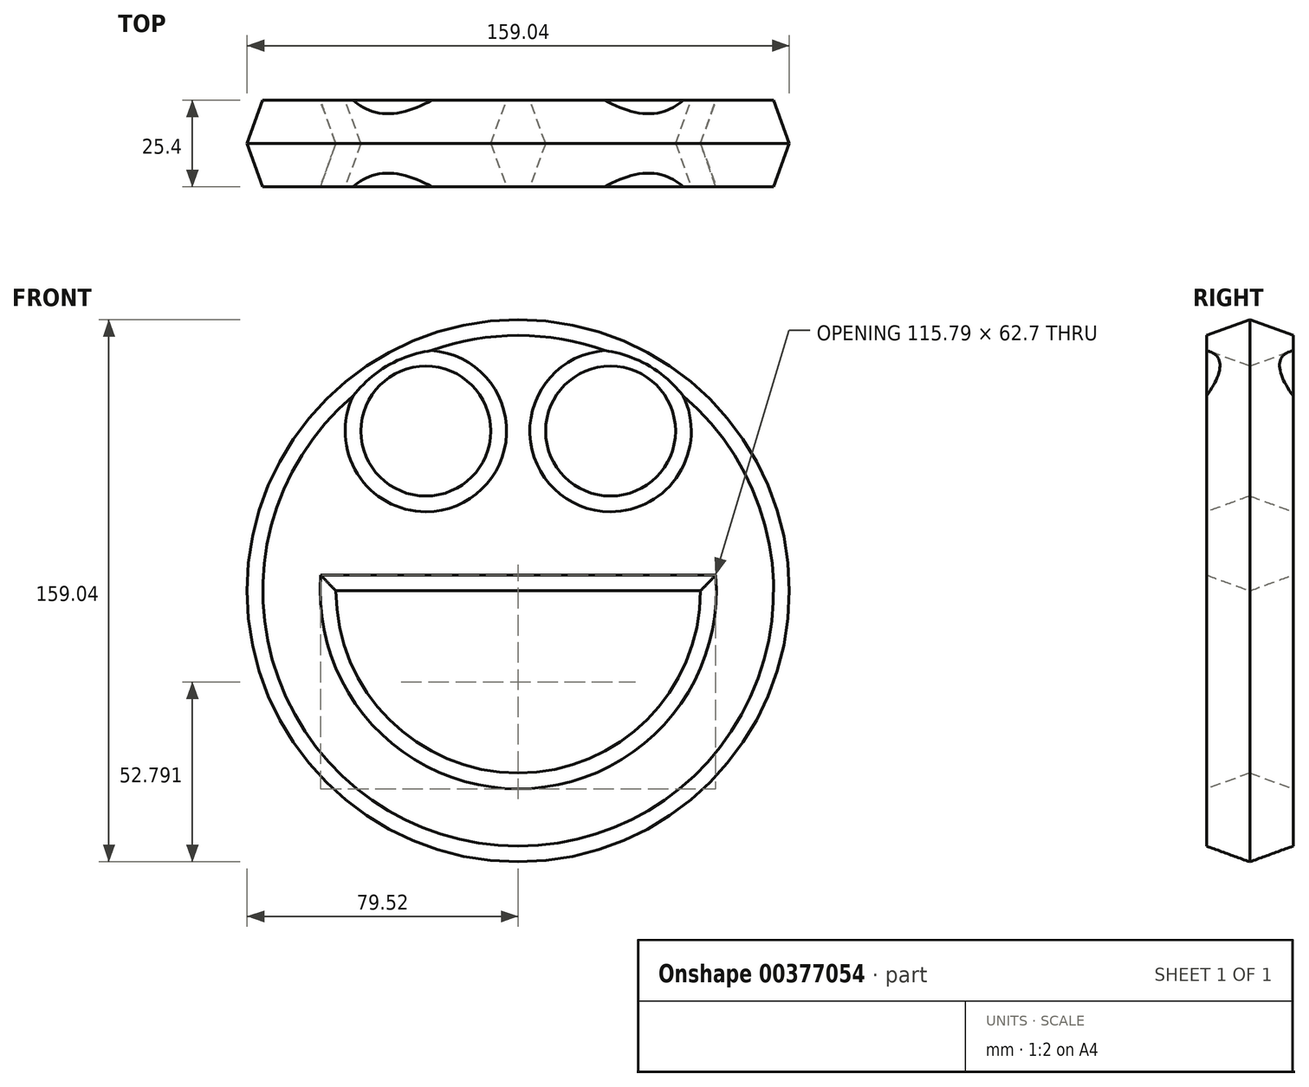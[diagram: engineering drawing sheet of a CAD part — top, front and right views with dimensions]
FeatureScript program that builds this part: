
annotation { "Feature Type Name" : "Feature", "Feature Type Description" : "" }
export const myFeature = defineFeature(function(context is Context, id is Id, definition is map)
    precondition{}
    {
        {
            var Q0;
            Q0=qCreatedBy(makeId("Front.planeOp"),FACE);
            var sketch = newSketch(context, id + "F0", { "sketchPlane" : qUnion([Q0])});
            skCircle(sketch, "E0", {"center": v(0, 0) * mm, "radius": 79.52 * mm});
            skArc(sketch, "E1", {"start": v(53.46, 0) * mm, "mid": v(0, -53.46) * mm, "end": v(-53.46, 0) * mm});
            skLineSegment(sketch, "E2", {"start": v(-53.46, 0) * mm, "end": v(53.46, 0) * mm});
            skCircle(sketch, "E3", {"center": v(-27.08, 46.86) * mm, "radius": 19.05 * mm});
            skCircle(sketch, "E4", {"center": v(27.08, 46.86) * mm, "radius": 19.05 * mm});
            skSolve(sketch);
        }
        {
            var Q0;
            Q0=makeQuery(id+"F0.imprint","IMPRINT",FACE,{"disambiguationData":[TD([[makeQuery(id+"F0.imprint","IMPRINT",EDGE,{"derivedFrom":sQuery(id+"F0.wireOp",EDGE,"E0")}),1.0]])]});
            extrude(context, id + "F1", {"entities" : qUnion([Q0]), "endBound" : BoundingType.SYMMETRIC, "depth" : 25.4 * mm, "hasDraft" : true, "draftAngle" : 20 * degree, "draftPullDirection" : true});
        }
    });
